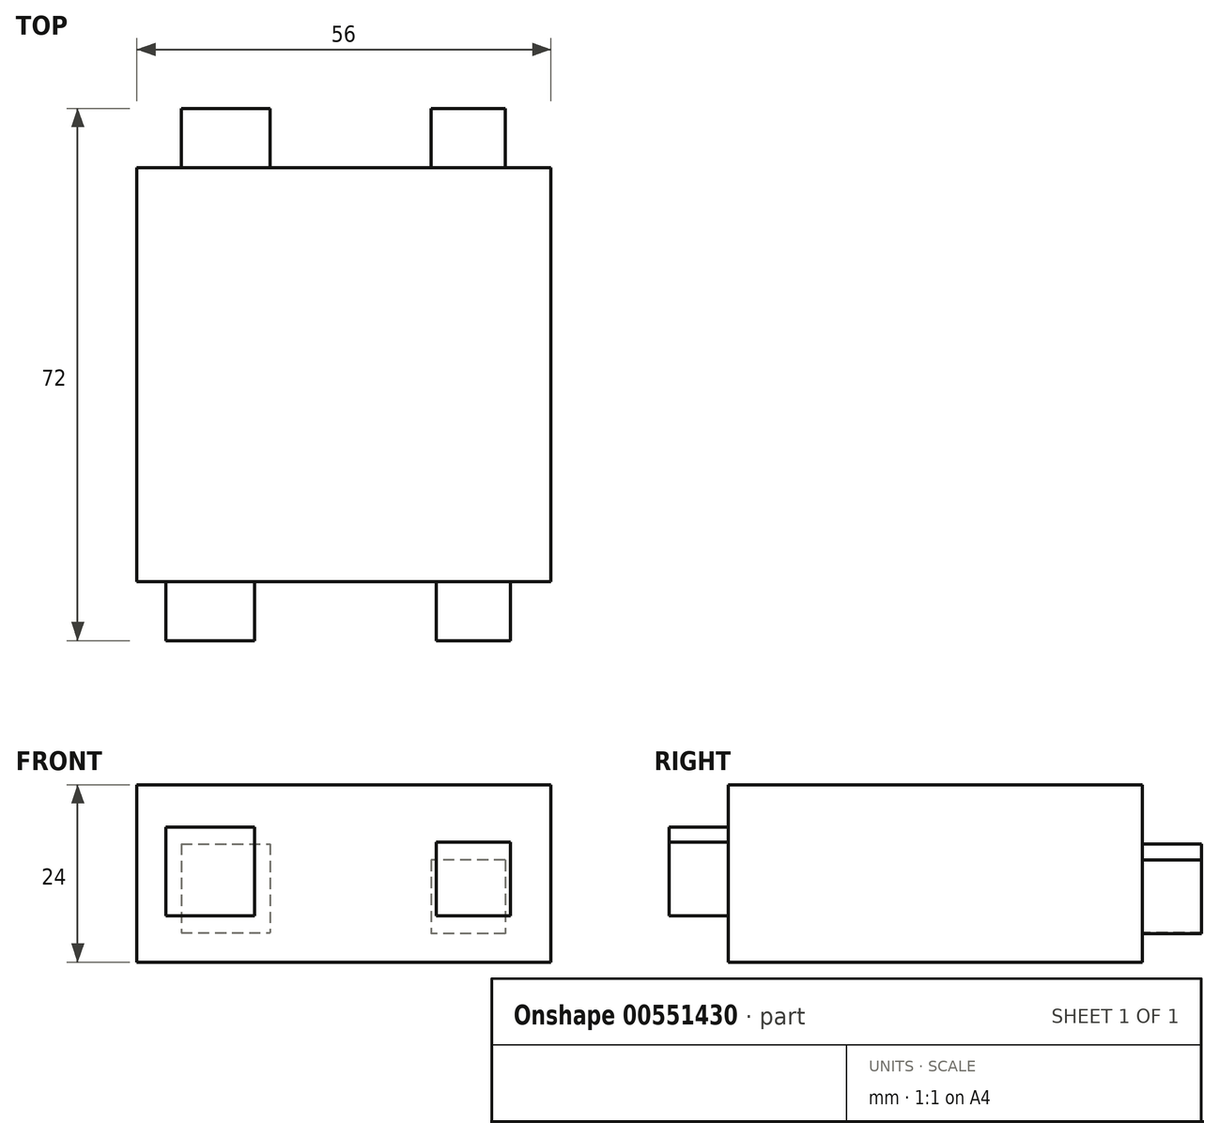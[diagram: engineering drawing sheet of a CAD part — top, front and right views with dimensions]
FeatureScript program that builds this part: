
annotation { "Feature Type Name" : "Feature", "Feature Type Description" : "" }
export const myFeature = defineFeature(function(context is Context, id is Id, definition is map)
    precondition{}
    {
        {
            var Q0;
            Q0=qCreatedBy(makeId("Top.planeOp"),FACE);
            var sketch = newSketch(context, id + "F0", { "sketchPlane" : qUnion([Q0])});
            skLineSegment(sketch, "E0.bottom", {"start": v(0, 0) * mm, "end": v(-28, 0) * mm});
            skLineSegment(sketch, "E0.top", {"start": v(0, -28) * mm, "end": v(-28, -28) * mm});
            skLineSegment(sketch, "E0.left", {"start": v(0, 0) * mm, "end": v(0, -28) * mm});
            skLineSegment(sketch, "E0.right", {"start": v(-28, 0) * mm, "end": v(-28, -28) * mm});
            skLineSegment(sketch, "E1.top", {"start": v(0, 28) * mm, "end": v(-28, 28) * mm});
            skLineSegment(sketch, "E1.left", {"start": v(0, 0) * mm, "end": v(0, 28) * mm});
            skLineSegment(sketch, "E1.right", {"start": v(-28, 0) * mm, "end": v(-28, 28) * mm});
            skLineSegment(sketch, "E2.bottom", {"start": v(0, 0) * mm, "end": v(28, 0) * mm});
            skLineSegment(sketch, "E2.top", {"start": v(0, 28) * mm, "end": v(28, 28) * mm});
            skLineSegment(sketch, "E2.right", {"start": v(28, 0) * mm, "end": v(28, 28) * mm});
            skLineSegment(sketch, "E3.top", {"start": v(0, -28) * mm, "end": v(28, -28) * mm});
            skLineSegment(sketch, "E3.right", {"start": v(28, 0) * mm, "end": v(28, -28) * mm});
            skSolve(sketch);
        }
        {
            var Q0;
            Q0=makeQuery(id+"F0.imprint","IMPRINT",FACE,{"disambiguationData":[TD([[makeQuery(id+"F0.imprint","IMPRINT",EDGE,{"derivedFrom":sQuery(id+"F0.wireOp",EDGE,"E0.top")}),-1.0]])]});
            var Q1;
            Q1=makeQuery(id+"F0.imprint","IMPRINT",FACE,{"disambiguationData":[TD([[makeQuery(id+"F0.imprint","IMPRINT",EDGE,{"derivedFrom":sQuery(id+"F0.wireOp",EDGE,"E2.bottom")}),-1.0]])]});
            var Q2;
            Q2=makeQuery(id+"F0.imprint","IMPRINT",FACE,{"disambiguationData":[TD([[makeQuery(id+"F0.imprint","IMPRINT",EDGE,{"derivedFrom":sQuery(id+"F0.wireOp",EDGE,"E2.top")}),-1.0]])]});
            var Q3;
            Q3=makeQuery(id+"F0.imprint","IMPRINT",FACE,{"disambiguationData":[TD([[makeQuery(id+"F0.imprint","IMPRINT",EDGE,{"derivedFrom":sQuery(id+"F0.wireOp",EDGE,"E0.bottom")}),-1.0]])]});
            extrude(context, id + "F1", {"entities" : qUnion([Q0, Q1, Q2, Q3]), "depth" : 24 * mm, "offsetDistance" : 25 * mm});
        }
        {
            var Q0;
            Q0=makeQuery(id+"F1.opExtrude","SWEPT_FACE",FACE,{"disambiguationData":[OSD([sQuery(id+"F0.wireOp",EDGE,"E1.top"),sQuery(id+"F0.wireOp",EDGE,"E2.top")])]});
            var sketch = newSketch(context, id + "F2", { "sketchPlane" : qUnion([Q0])});
            skLineSegment(sketch, "E4.bottom", {"start": v(-21.82, 13.82) * mm, "end": v(-11.82, 13.82) * mm});
            skLineSegment(sketch, "E4.top", {"start": v(-21.82, 3.82) * mm, "end": v(-11.82, 3.82) * mm});
            skLineSegment(sketch, "E4.left", {"start": v(-21.82, 13.82) * mm, "end": v(-21.82, 3.82) * mm});
            skLineSegment(sketch, "E4.right", {"start": v(-11.82, 13.82) * mm, "end": v(-11.82, 3.82) * mm});
            skLineSegment(sketch, "E5.bottom", {"start": v(22, 15.99) * mm, "end": v(10, 15.99) * mm});
            skLineSegment(sketch, "E5.top", {"start": v(22, 3.99) * mm, "end": v(10, 3.99) * mm});
            skLineSegment(sketch, "E5.left", {"start": v(22, 15.99) * mm, "end": v(22, 3.99) * mm});
            skLineSegment(sketch, "E5.right", {"start": v(10, 15.99) * mm, "end": v(10, 3.99) * mm});
            skSolve(sketch);
        }
        {
            var Q0;
            Q0=makeQuery(id+"F2.imprint","IMPRINT",FACE,{"disambiguationData":[TD([[makeQuery(id+"F2.imprint","IMPRINT",EDGE,{"derivedFrom":sQuery(id+"F2.wireOp",EDGE,"E4.bottom")}),-1.0]])]});
            var Q1;
            Q1=makeQuery(id+"F2.imprint","IMPRINT",FACE,{"disambiguationData":[TD([[makeQuery(id+"F2.imprint","IMPRINT",EDGE,{"derivedFrom":sQuery(id+"F2.wireOp",EDGE,"E5.bottom")}),1.0]])]});
            extrude(context, id + "F3", {"entities" : qUnion([Q0, Q1]), "operationType" : NewBodyOperationType.ADD, "depth" : 8 * mm, "offsetDistance" : 25 * mm});
        }
        {
            var Q0;
            Q0=makeQuery(id+"F1.opExtrude","SWEPT_FACE",FACE,{"disambiguationData":[OSD([sQuery(id+"F0.wireOp",EDGE,"E0.top"),sQuery(id+"F0.wireOp",EDGE,"E3.top")])]});
            var sketch = newSketch(context, id + "F4", { "sketchPlane" : qUnion([Q0])});
            skLineSegment(sketch, "E6.bottom", {"start": v(-24.08, 18.25) * mm, "end": v(-12.08, 18.25) * mm});
            skLineSegment(sketch, "E6.top", {"start": v(-24.08, 6.25) * mm, "end": v(-12.08, 6.25) * mm});
            skLineSegment(sketch, "E6.left", {"start": v(-24.08, 18.25) * mm, "end": v(-24.08, 6.25) * mm});
            skLineSegment(sketch, "E6.right", {"start": v(-12.08, 18.25) * mm, "end": v(-12.08, 6.25) * mm});
            skLineSegment(sketch, "E7.bottom", {"start": v(12.5, 6.25) * mm, "end": v(22.5, 6.25) * mm});
            skLineSegment(sketch, "E7.top", {"start": v(12.5, 16.25) * mm, "end": v(22.5, 16.25) * mm});
            skLineSegment(sketch, "E7.left", {"start": v(12.5, 6.25) * mm, "end": v(12.5, 16.25) * mm});
            skLineSegment(sketch, "E7.right", {"start": v(22.5, 6.25) * mm, "end": v(22.5, 16.25) * mm});
            skSolve(sketch);
        }
        {
            var Q0;
            Q0 = qSketchRegion(id + "F4", true);
            extrude(context, id + "F5", {"entities" : qUnion([Q0]), "operationType" : NewBodyOperationType.ADD, "depth" : 8 * mm, "offsetDistance" : 25 * mm});
        }
    });
